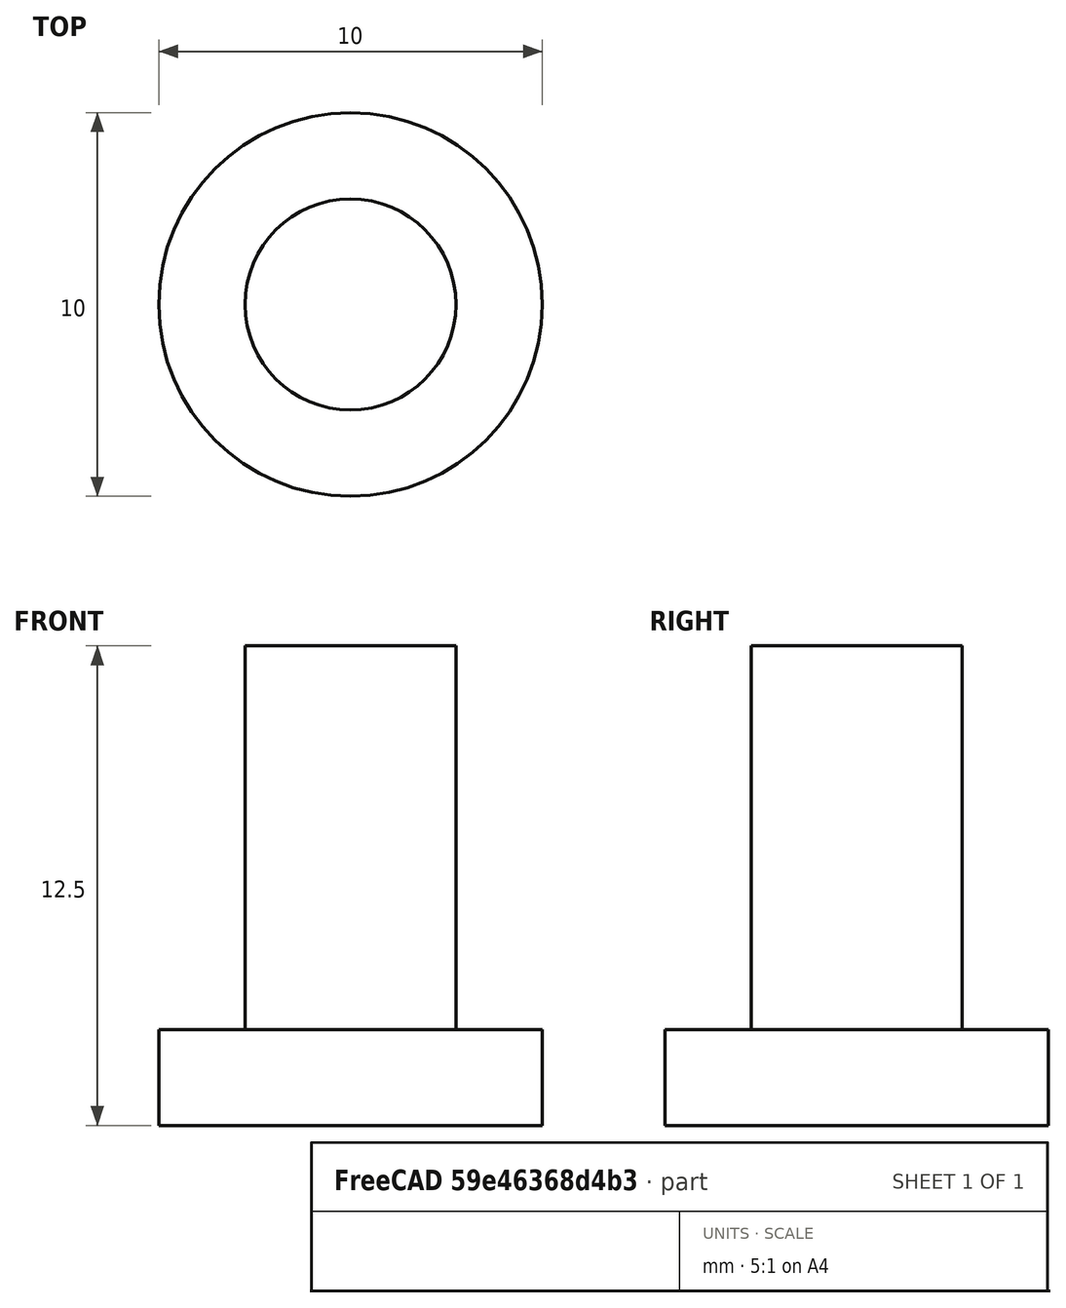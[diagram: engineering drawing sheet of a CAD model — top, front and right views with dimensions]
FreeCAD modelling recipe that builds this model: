
FCSTD DOCUMENT  (FreeCAD 0.19R24267 +148 (Git))
Label: cablePlug
License: All rights reserved
LicenseURL: http://en.wikipedia.org/wiki/All_rights_reserved
objects: Sketcher::SketchObject×1, PartDesign::Revolution×1, PartDesign::Body×1
note: 4 computed .brp shape members not serialized (recipe doc carries the construction recipe); baked Part::Feature solids carry a one-line shape summary decoded from their .brp

FEATURE [Sketcher::SketchObject] Sketch
  FullyConstrained = true
  MapMode = 5
  Placement = pos=(0,0,0) rot=(1,0,0;1.5708rad)
  Support = -> [XZ_Plane]
  sketch-geometry (6):
    g0: LineSegment StartX=0 StartY=12.5 StartZ=0 EndX=2.75 EndY=12.5 EndZ=0
    g1: LineSegment StartX=2.75 StartY=12.5 StartZ=0 EndX=2.75 EndY=2.5 EndZ=0
    g2: LineSegment StartX=2.75 StartY=2.5 StartZ=0 EndX=5 EndY=2.5 EndZ=0
    g3: LineSegment StartX=5 StartY=2.5 StartZ=0 EndX=5 EndY=0 EndZ=0
    g4: LineSegment StartX=0 StartY=0 StartZ=0 EndX=5 EndY=0 EndZ=0
    g5: LineSegment StartX=0 StartY=12.5 StartZ=0 EndX=0 EndY=0 EndZ=0
  constraints (17):
    c: PointOnObject(g0,g-2)
    c: Horizontal(g0)
    c: Coincident(g1,g0)
    c: Vertical(g1)
    c: Coincident(g2,g1)
    c: Horizontal(g2)
    c: Coincident(g3,g2)
    c: Vertical(g3)
    c: Coincident(g4,g-1)
    c: Horizontal(g4)
    c: Coincident(g4,g3)
    c: Coincident(g5,g0)
    c: Coincident(g5,g4)
    c: DistanceX(g0,g0) = 2.75
    c: DistanceX(g4,g4) = 5
    c: DistanceY(g1,g1) = 10
    c: DistanceY(g3,g3) = 2.5
FEATURE [PartDesign::Revolution] Revolution
  Angle = 360
  Axis = (0,2e-16,1)
  Base = (0,0,0)
  Placement = pos=(0,0,0) rot=(1,0,0;1.5708rad)
  Profile = -> Sketch
  ReferenceAxis = -> Sketch [V_Axis]
  Reversed = true
FEATURE [PartDesign::Body] Body
  Group = -> [Sketch,Revolution]
  Origin = -> Origin
  Tip = -> Revolution
